# Revit family: CENTRA BIM 130831
name_source: partatom
category: Air Terminals
revit_build: Autodesk Revit MEP 2013 (Build: 20120221_2030(x64)
units: mm (PartAtom-declared; Revit-internal decimal feet)

## types (9) — shared parameters
AC Frequency Input = 50Hz nominal
AC Voltage Input = 240
Accessories = 150mm Conversion Kit - 443334, White Wall Kit - 245102,Brown Wall Kit - 254100, Window Kit - 442947 , Ceiling Kit - 443800
Country of Manufacture = UK
Default Elevation = 1200 mm
Depth = 722 mm  [stored 2.36877 ft]
Grille Depth = 35 mm  [stored 0.114829 ft]
Height = 160 mm  [stored 0.524934 ft]
IP Rating = IPX4
Manufacturer - Name = Vent-Axia Ltd
Manufacturer - Website = www.vent-axia.com
Motor Rating = 2.4 W (max)
Operating Temperature = (-5C to +40C)
Operational and Maintenance Manual = http://www.vent-axia.com
Spigot Depth = 115 mm  [stored 0.377297 ft]
Sub Type = dMEV
Warranty period = Unit 2 years                                    Motor 5 years
Weight = 0.7kg
Width = 160 mm  [stored 0.524934 ft]

## per-type parameters (varying)
| type | Category | Controllers Supply | Fan Unit Supply | Part Number | Product Description | Spigot Diameter |
| Centra | Lo Carbon Centra |  |  | 441782 | Lo Carbon Centra | 99 mm  [stored 0.324803 ft] |
| Centra T | Lo Carbon Centra |  |  | 442954 | Lo Carbon Centra with built in adjustable overun timer | 99 mm  [stored 0.324803 ft] |
| Centra TP | Lo Carbon Centra |  |  | 447127 | Lo Carbon Centra with built in adjustable overun timer & pullcord override | 100 mm  [stored 0.328084 ft] |
| Centra HT | Lo Carbon Centra |  |  | 442955 | Lo Carbon Centra with built in humidistat & adjustable overun timer | 99 mm  [stored 0.324803 ft] |
| Centra HTP | Lo Carbon Centra |  |  | 443045 | Lo Carbon Centra with built in humidistat & adjustable overun timer .  Pullcord override | 99 mm  [stored 0.324803 ft] |
| Centra SELV T | Lo Carbon Centra SELV | 12V DC SELV | 220-240 V AC with 12V DC SELV OUTPUT | 443175 | Lo Carbon Centra SELV with built in adjustable overun timer | 99 mm  [stored 0.324803 ft] |
| Centra SELV TP | Lo Carbon Centra SELV | 12V DC SELV | 220-240 V AC with 12V DC SELV OUTPUT | 447128 | Lo Carbon Centra SELV with built in adjustable overun timer & pullcord override | 99 mm  [stored 0.324803 ft] |
| Centra SELV HT | Lo Carbon Centra SELV | 12V DC SELV | 220-240 V AC with 12V DC SELV OUTPUT | 443176 | Lo Carbon Centra SELV with built in humidistat & adjustable overun timer | 99 mm  [stored 0.324803 ft] |
| Centra SELV HTP | Lo Carbon Centra SELV | 12V DC SELV | 220-240 V AC with 12V DC SELV OUTPUT | 443177 | Lo Carbon Centra SELV with built in humidistat & adjustable overun timer .  Pullcord override | 99 mm  [stored 0.324803 ft] |

note: column(s) folded — value = type name in every type: Family

note: source unit labels omitted for AC Voltage Input — the stored unit's dimension contradicts the parameter name (converter mislabeling)

note: [stored X ft] marks values corroborated as IEEE doubles in the binary element streams (Revit-internal decimal feet)

## geometry (parser evidence)
native form markers: Sweep x1
no freeform markers — native parametric forms only
